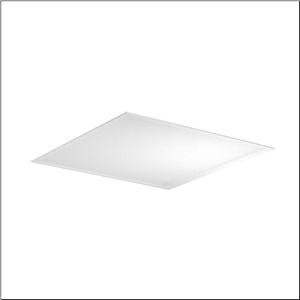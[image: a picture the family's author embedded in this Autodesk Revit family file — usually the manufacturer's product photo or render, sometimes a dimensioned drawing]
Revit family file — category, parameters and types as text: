
# Revit family: apollon_r__31_square_51mp12wd2n42_b6b6
name_source: partatom
category: Lighting Fixtures
units: mm (PartAtom-declared; Revit-internal decimal feet)

## family parameters
Cut with Voids When Loaded = No
Host = Face
Light Source = No
Part Type = Normal
Room Calculation Point = No
Round Connector Dimension = Use Diameter
Shared = No

## types (1)
- --- (1 x LED, 4000 lm, 27.5 W, 5000K)
    Apparent Load = 28 VA
    CIE Flux Codes = 62 87 97 100 100
    Color Rendering = 80
    Color Temperature = 5000K
    Default Elevation = 1800 mm
    Description = Apollon® 31 square, office luminaire, primary optical cover: micro prismatic cover, of PMMA, CAT 2 (L<= 3000cd/m²), light emission: direct distribution, primary light characteristic: symmetric, installation type: lay-in mounting, LED, rated luminous flux: 4.000lm, luminous efficacy: 145lm/W, light colour: 840/850, colour temperature: 4000/5000K, with terminal, 5-pole, mains connection: 220..240V, AC/DC, 0/50..60Hz, rated input power: 28W, housing, of aluminium, traffic white (RAL 9016), module: M600, length: 595mm, width: 595mm, height: 32mm, housing upper side, of sheet steel, galvanised, protection rating (complete): IP20, protection rating (on room side): IP40, insulation class (complete): insulation class II (safety insulation), certification: CE, ENEC, impact resistance: IK03, permissible operating ambient temperature: -20..+40°C, permissible storage temperature: -20..+60°C, packaging unit: 1 piece
    Height = 0 mm  [stored 0 ft]
    Lamp = 1 x LED
    Lamp Light Flux = 4000 lm
    Lamp Power = 27.5 W
    Lamp count = 1
    Length = 595 mm
    Luminous efficacy = 145 lm/W
    Manufacturer = Siteco
    ModVariant = No
    Model = 51MP12WD2N42
    Mounting Place = Ceiling
    Mounting Type = Recessed
    Number of Poles = 1
    OnlyDefault = Yes
    Power Factor = 1
    Product Name = Apollon® 31 square
    Product group = office luminaire | ceiling recessed
    ProductGroupID = 401
    Protection Class = Protection class II
    Protection Degree = IP 20
    RLX_Detail_Level = 1
    RLX_Emergency_Light_Flux = 0 lm
    RLX_Emergency_Type = 0
    RLX_Emergency_Type_DB = No
    RlxData = <blob elided: 12709 chars, md5=0239aa55>
    Socket = socket
    Standby Power = 0 W
    System Light Flux = 4000 lm
    System Power = 28 W
    Type Comments = individual setting: colour temperature 5000K
    Type Image = l_1291035.jpg
    URL = http://relux.com
    VarID = @adj_008989
    Voltage = 0 V
    Weight = 0.00 kg
    Width = 595 mm

note: [stored X ft] marks values corroborated as IEEE doubles in the binary element streams (Revit-internal decimal feet)

## geometry (parser evidence)
native form markers: Sweep x10
no freeform markers — native parametric forms only
